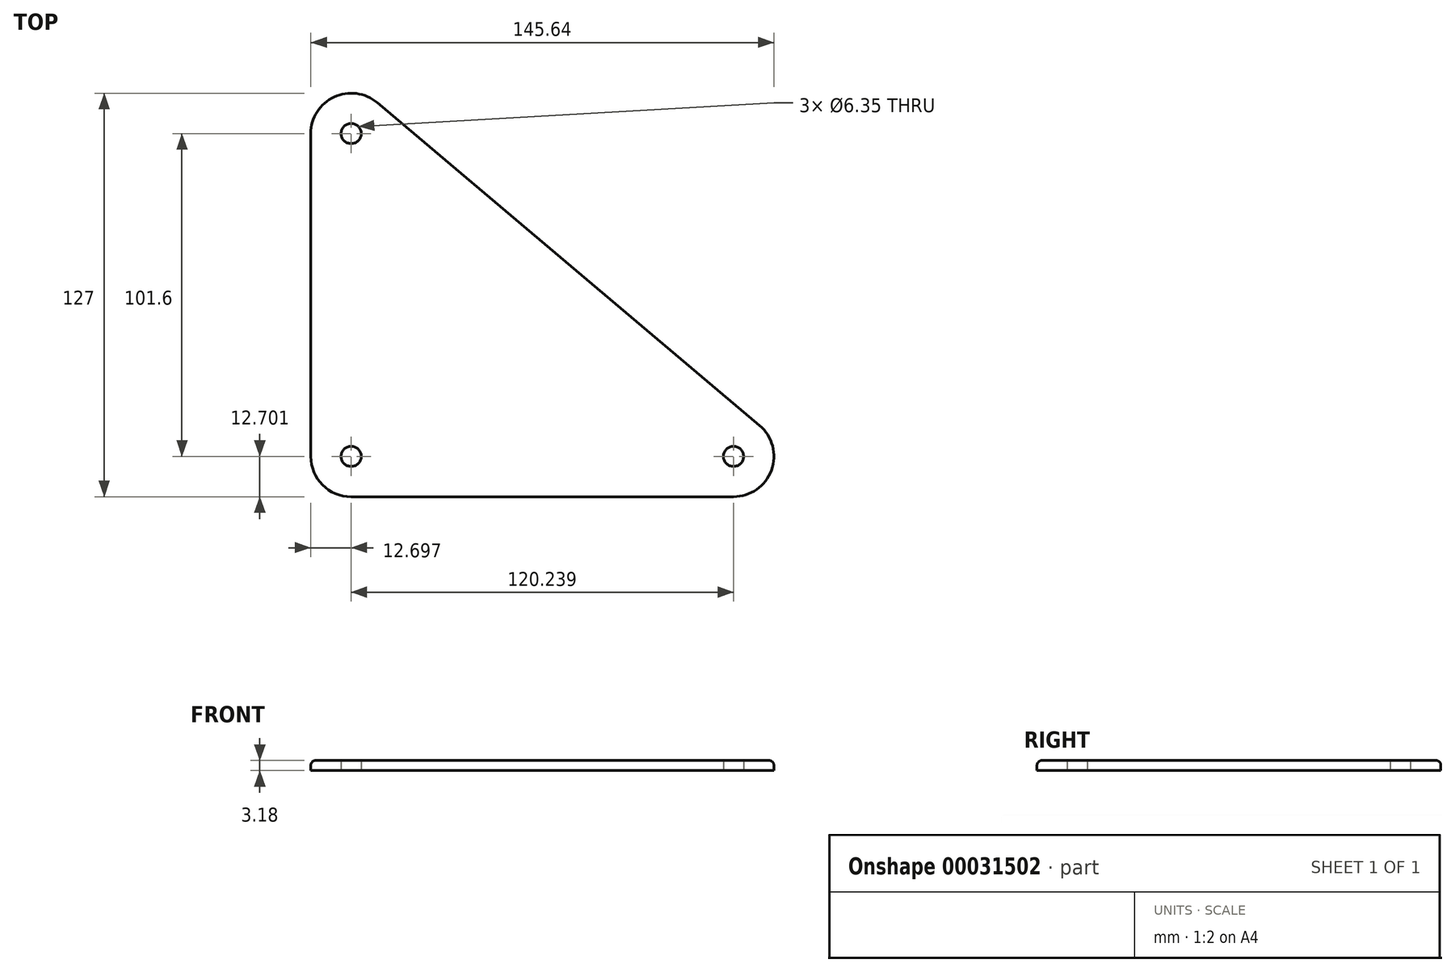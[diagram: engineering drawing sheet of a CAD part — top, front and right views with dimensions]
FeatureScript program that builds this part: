
annotation { "Feature Type Name" : "Feature", "Feature Type Description" : "" }
export const myFeature = defineFeature(function(context is Context, id is Id, definition is map)
    precondition{}
    {
        {
            var Q0;
            Q0=qCreatedBy(makeId("Top.planeOp"),FACE);
            var sketch = newSketch(context, id + "F0", { "sketchPlane" : qUnion([Q0])});
            skLineSegment(sketch, "E0.rect.top", {"start": v(49.12, -70.83) * mm, "end": v(-71.12, -70.83) * mm});
            skLineSegment(sketch, "E0.rect.right", {"start": v(-83.82, 43.47) * mm, "end": v(-83.82, -58.13) * mm});
            skPoint(sketch, "E0.rect.middle", {"position": v(0, 0) * mm});
            skLineSegment(sketch, "E1", {"start": v(-62.93, 53.17) * mm, "end": v(57.31, -48.43) * mm});
            skPoint(sketch, "E2.visualSharp", {"position": v(-83.82, 70.83) * mm});
            skArc(sketch, "E2.filletArc", {"start": v(-62.93, 53.17) * mm, "mid": v(-76.47, 55) * mm, "end": v(-83.82, 43.47) * mm});
            skPoint(sketch, "E3.visualSharp", {"position": v(83.82, -70.83) * mm});
            skArc(sketch, "E3.filletArc", {"start": v(49.12, -70.83) * mm, "mid": v(61.04, -62.5) * mm, "end": v(57.31, -48.43) * mm});
            skPoint(sketch, "E4.visualSharp", {"position": v(-83.82, -70.83) * mm});
            skArc(sketch, "E4.filletArc", {"start": v(-83.82, -58.13) * mm, "mid": v(-80.1, -67.1) * mm, "end": v(-71.12, -70.83) * mm});
            skCircle(sketch, "E5", {"center": v(49.12, -58.13) * mm, "radius": 3.18 * mm});
            skCircle(sketch, "E6", {"center": v(-71.12, -58.13) * mm, "radius": 3.18 * mm});
            skCircle(sketch, "E7", {"center": v(-71.12, 43.47) * mm, "radius": 3.18 * mm});
            skSolve(sketch);
        }
        {
            var Q0;
            Q0=makeQuery(id+"F0.imprint","IMPRINT",FACE,{"disambiguationData":[TD([[makeQuery(id+"F0.imprint","IMPRINT",EDGE,{"derivedFrom":sQuery(id+"F0.wireOp",EDGE,"E0.rect.top")}),-1.0]])]});
            extrude(context, id + "F1", {"entities" : qUnion([Q0]), "depth" : 3.17 * mm});
        }
        {
            var Q0;
            Q0=makeQuery(id+"F1.opExtrude","CAP_EDGE",EDGE,{"disambiguationData":[OSD([sQuery(id+"F0.wireOp",EDGE,"E0.rect.right")])],"isStart":false});
            fillet(context, id + "F2", {"entities" : qUnion([Q0]), "radius" : 1.52 * mm, "tangentPropagation" : true, "allowEdgeOverflow" : false});
        }
    });
